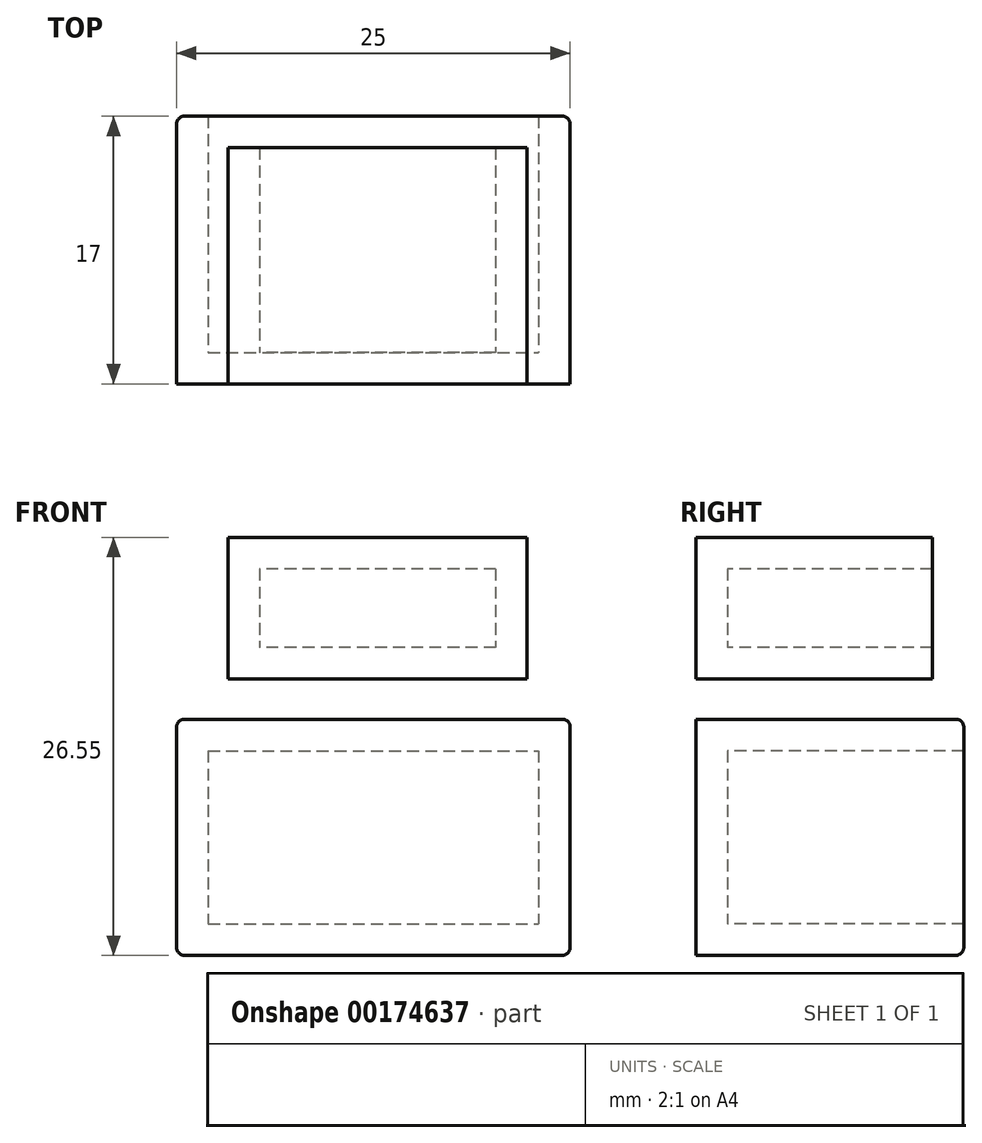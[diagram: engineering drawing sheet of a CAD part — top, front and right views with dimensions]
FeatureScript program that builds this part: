
annotation { "Feature Type Name" : "Feature", "Feature Type Description" : "" }
export const myFeature = defineFeature(function(context is Context, id is Id, definition is map)
    precondition{}
    {
        {
            var Q0;
            Q0=qCreatedBy(makeId("Front.planeOp"),FACE);
            var sketch = newSketch(context, id + "F0", { "sketchPlane" : qUnion([Q0])});
            skLineSegment(sketch, "E0.bottom", {"start": v(-10.76, 8.29) * mm, "end": v(14.24, 8.29) * mm});
            skLineSegment(sketch, "E0.top", {"start": v(-10.76, -6.71) * mm, "end": v(14.24, -6.71) * mm});
            skLineSegment(sketch, "E0.left", {"start": v(-10.76, 8.29) * mm, "end": v(-10.76, -6.71) * mm});
            skLineSegment(sketch, "E0.right", {"start": v(14.24, 8.29) * mm, "end": v(14.24, -6.71) * mm});
            skSolve(sketch);
        }
        {
            var Q0;
            Q0 = qSketchRegion(id + "F0", true);
            extrude(context, id + "F1", {"entities" : qUnion([Q0]), "depth" : 2 * mm});
        }
        {
            var Q0;
            Q0=makeQuery(id+"F1.opExtrude","CAP_FACE",FACE,{"disambiguationData":[OSD([sQuery(id+"F0.wireOp",EDGE,"E0.bottom"),sQuery(id+"F0.wireOp",EDGE,"E0.top"),sQuery(id+"F0.wireOp",EDGE,"E0.left"),sQuery(id+"F0.wireOp",EDGE,"E0.right")])],"isStart":true});
            var sketch = newSketch(context, id + "F2", { "sketchPlane" : qUnion([Q0])});
            skLineSegment(sketch, "E1.0", {"start": v(10.76, -6.71) * mm, "end": v(-14.24, -6.71) * mm});
            skLineSegment(sketch, "E2.0", {"start": v(-14.24, 8.29) * mm, "end": v(-14.24, -6.71) * mm});
            skLineSegment(sketch, "E3.0", {"start": v(10.76, 8.29) * mm, "end": v(-14.24, 8.29) * mm});
            skLineSegment(sketch, "E4.0", {"start": v(10.76, 8.29) * mm, "end": v(10.76, -6.71) * mm});
            skLineSegment(sketch, "E5.0", {"start": v(8.76, 6.29) * mm, "end": v(8.76, -4.71) * mm});
            skLineSegment(sketch, "E5.1", {"start": v(8.76, 6.29) * mm, "end": v(-12.24, 6.29) * mm});
            skLineSegment(sketch, "E5.2", {"start": v(-12.24, 6.29) * mm, "end": v(-12.24, -4.71) * mm});
            skLineSegment(sketch, "E5.3", {"start": v(8.76, -4.71) * mm, "end": v(-12.24, -4.71) * mm});
            skSolve(sketch);
        }
        {
            var Q0;
            Q0=makeQuery(id+"F2.imprint","IMPRINT",FACE,{"disambiguationData":[TD([[makeQuery(id+"F2.imprint","IMPRINT",EDGE,{"derivedFrom":sQuery(id+"F2.wireOp",EDGE,"E1.0")}),-1.0]])]});
            extrude(context, id + "F3", {"entities" : qUnion([Q0]), "operationType" : NewBodyOperationType.ADD, "depth" : 15 * mm});
        }
        {
            var Q0;
            Q0=makeQuery(id+"F3.opExtrude","CAP_EDGE",EDGE,{"disambiguationData":[OSD([sQuery(id+"F2.wireOp",EDGE,"E3.0")])],"isStart":false});
            var Q1;
            Q1=makeQuery(id+"F3.opExtrude","CAP_EDGE",EDGE,{"disambiguationData":[OSD([sQuery(id+"F2.wireOp",EDGE,"E1.0")])],"isStart":false});
            fillet(context, id + "F4", {"entities" : qUnion([Q0, Q1]), "radius" : 0.5 * mm, "tangentPropagation" : true, "allowEdgeOverflow" : false});
        }
        {
            var Q0;
            Q0=makeQuery(id+"F3.opExtrude","CAP_EDGE",EDGE,{"disambiguationData":[OSD([sQuery(id+"F2.wireOp",EDGE,"E2.0")])],"isStart":false});
            var Q1;
            Q1=makeQuery(id+"F3.opExtrude","CAP_EDGE",EDGE,{"disambiguationData":[OSD([sQuery(id+"F2.wireOp",EDGE,"E4.0")])],"isStart":false});
            fillet(context, id + "F5", {"entities" : qUnion([Q0, Q1]), "radius" : 0.5 * mm, "tangentPropagation" : true, "allowEdgeOverflow" : false});
        }
        {
            var Q0;
            Q0=qCreatedBy(makeId("Front.planeOp"),FACE);
            var sketch = newSketch(context, id + "F6", { "sketchPlane" : qUnion([Q0])});
            skLineSegment(sketch, "E6.bottom", {"start": v(11.5, 19.84) * mm, "end": v(-7.5, 19.84) * mm});
            skLineSegment(sketch, "E6.top", {"start": v(11.5, 10.84) * mm, "end": v(-7.5, 10.84) * mm});
            skLineSegment(sketch, "E6.left", {"start": v(11.5, 19.84) * mm, "end": v(11.5, 10.84) * mm});
            skLineSegment(sketch, "E6.right", {"start": v(-7.5, 19.84) * mm, "end": v(-7.5, 10.84) * mm});
            skSolve(sketch);
        }
        {
            var Q0;
            Q0=makeQuery(id+"F6.imprint","IMPRINT",FACE,{"disambiguationData":[TD([[makeQuery(id+"F6.imprint","IMPRINT",EDGE,{"derivedFrom":sQuery(id+"F6.wireOp",EDGE,"E6.bottom")}),1.0]])]});
            extrude(context, id + "F7", {"entities" : qUnion([Q0]), "depth" : 2 * mm});
        }
        {
            var Q0;
            Q0=qCreatedBy(makeId("Front.planeOp"),FACE);
            var sketch = newSketch(context, id + "F8", { "sketchPlane" : qUnion([Q0])});
            skPoint(sketch, "E7.0", {"position": v(11.5, 15.34) * mm});
            skLineSegment(sketch, "E8.0", {"start": v(11.5, 10.84) * mm, "end": v(-7.5, 10.84) * mm});
            skPoint(sketch, "E9.0", {"position": v(-7.5, 15.34) * mm});
            skLineSegment(sketch, "E10.0", {"start": v(11.5, 19.84) * mm, "end": v(-7.5, 19.84) * mm});
            skLineSegment(sketch, "E11.0", {"start": v(11.5, 19.84) * mm, "end": v(11.5, 10.84) * mm});
            skLineSegment(sketch, "E12.0", {"start": v(-7.5, 19.84) * mm, "end": v(-7.5, 10.84) * mm});
            skLineSegment(sketch, "E13.0", {"start": v(9.5, 17.84) * mm, "end": v(9.5, 12.84) * mm});
            skLineSegment(sketch, "E13.1", {"start": v(9.5, 17.84) * mm, "end": v(-5.5, 17.84) * mm});
            skLineSegment(sketch, "E13.2", {"start": v(-5.5, 17.84) * mm, "end": v(-5.5, 12.84) * mm});
            skLineSegment(sketch, "E13.3", {"start": v(9.5, 12.84) * mm, "end": v(-5.5, 12.84) * mm});
            skSolve(sketch);
        }
        {
            var Q0;
            Q0=makeQuery(id+"F8.imprint","IMPRINT",FACE,{"disambiguationData":[TD([[makeQuery(id+"F8.imprint","IMPRINT",EDGE,{"derivedFrom":sQuery(id+"F8.wireOp",EDGE,"E8.0")}),-1.0]])]});
            extrude(context, id + "F9", {"entities" : qUnion([Q0]), "operationType" : NewBodyOperationType.ADD, "oppositeDirection" : true, "depth" : 13 * mm});
        }
    });
